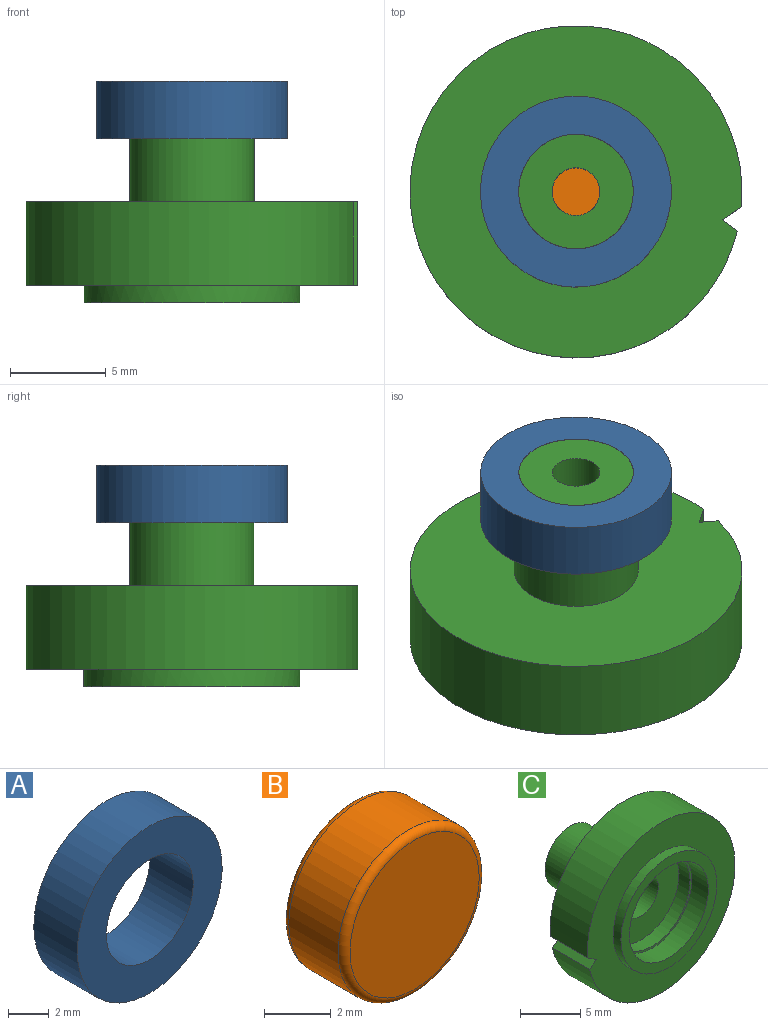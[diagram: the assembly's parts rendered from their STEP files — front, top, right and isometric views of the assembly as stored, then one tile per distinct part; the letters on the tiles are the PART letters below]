
ASSEMBLY  parts=3 mates=4
PART A: 4 faces, bbox 10x3x10 mm
  f0: plane 10x10mm, normal (0,1,0), area 50.3mm2, adj f2,f3
  f1: plane 10x10mm, normal (0,-1,0), area 50.3mm2, adj f2,f3
  f2: cylinder r=5mm len=10mm, axis (0,-1,0), area 94.2mm2, adj f0,f1
  f3: cylinder r=3mm len=6mm, axis (0,-1,0), area 56.5mm2, adj f0,f1
PART B: 5 faces, bbox 6.5x2.6x6.5 mm
  f0: cylinder r=3mm len=6mm, axis (0,-1,0), area 39.4mm2, adj f3,f4
  f1: plane 5.49x5.49mm, normal (0,1,0), area 23.7mm2, adj f4
  f2: plane 5.49x5.49mm, normal (0,-1,0), area 23.7mm2, adj f3
  f3: torus R=2.75mm, axis (0,1,0), area 7.3mm2, adj f0,f2
  f4: torus R=2.75mm, axis (0,1,0), area 7.3mm2, adj f0,f1
PART C: 18 faces, bbox 17.4x11.6x17.4 mm
  f0: cylinder r=1.25mm len=6.34mm, axis (0,1,0), area 49.8mm2, adj f15,f17
  f1: cylinder r=3mm len=6mm, axis (0,-1,0), area 56.5mm2, adj f14,f17
  f2: plane 17.39x17.39mm, normal (0,1,0), area 203.7mm2, adj f4,f5,f6,f13
  f3: plane 17.39x17.39mm, normal (0,-1,0), area 136.6mm2, adj f4,f5,f6,f9
  f4: plane 4.39x0.8mm, normal (-0.6,0,0.8), area 4.4mm2, adj f2,f3,f5,f6
  f5: plane 4.39x1.01mm, normal (-0.56,0,-0.83), area 5.3mm2, adj f2,f3,f4,f6
  f6: cylinder r=8.7mm len=17.39mm, axis (0,-1,0), area 234.1mm2, adj f2,f3,f4,f5
  f7: cylinder r=4.65mm len=9.3mm, axis (0,-1,0), area 57mm2, adj f8,f11
  f8: plane 11.3x11.3mm, normal (0,-1,0), area 32.4mm2, adj f7,f9
  f9: cylinder r=5.65mm len=11.3mm, axis (0,1,0), area 31.9mm2, adj f3,f8
  f10: cylinder r=4.45mm len=8.9mm, axis (0,1,0), area 36.3mm2, adj f11,f12
  f11: plane 9.3x9.3mm, normal (0,-1,0), area 5.7mm2, adj f7,f10
  f12: plane 8.9x8.9mm, normal (0,-1,0), area 49.6mm2, adj f10,f16
  f13: cylinder r=3.25mm len=6.5mm, axis (0,-1,0), area 67.4mm2, adj f2,f14
  f14: plane 6.5x6.5mm, normal (0,1,0), area 4.9mm2, adj f1,f13
  f15: plane 4x4mm, normal (0,-1,0), area 7.7mm2, adj f0,f16
  f16: cylinder r=2mm len=4mm, axis (0,-1,0), area 25.1mm2, adj f12,f15
  f17: plane 6x6mm, normal (0,1,0), area 23.4mm2, adj f0,f1
PLACE A rot(axis=(-0.58,0.58,-0.58),120deg) t=(0,0,0)mm
PLACE B rot(axis=(0.58,-0.58,-0.58),120deg) t=(0,0,-10.94)mm
PLACE C rot(axis=(0,0.71,0.71),180deg) t=(0,0,-10.69)mm
MATE cylindrical C.f0 <-> A.f2  axis (0,0,-1) through (0,0,-1.5)mm
MATE planar B.f0 <-> C.f0  axis (0,0,1) through (0,0,-8.34)mm
MATE fastened A.f2 <-> C.f0  axis (0,0,-1) through (0,0,-3)mm
MATE cylindrical B.f0 <-> C.f0  axis (0,0,-1) through (0,0,-10.68)mm
